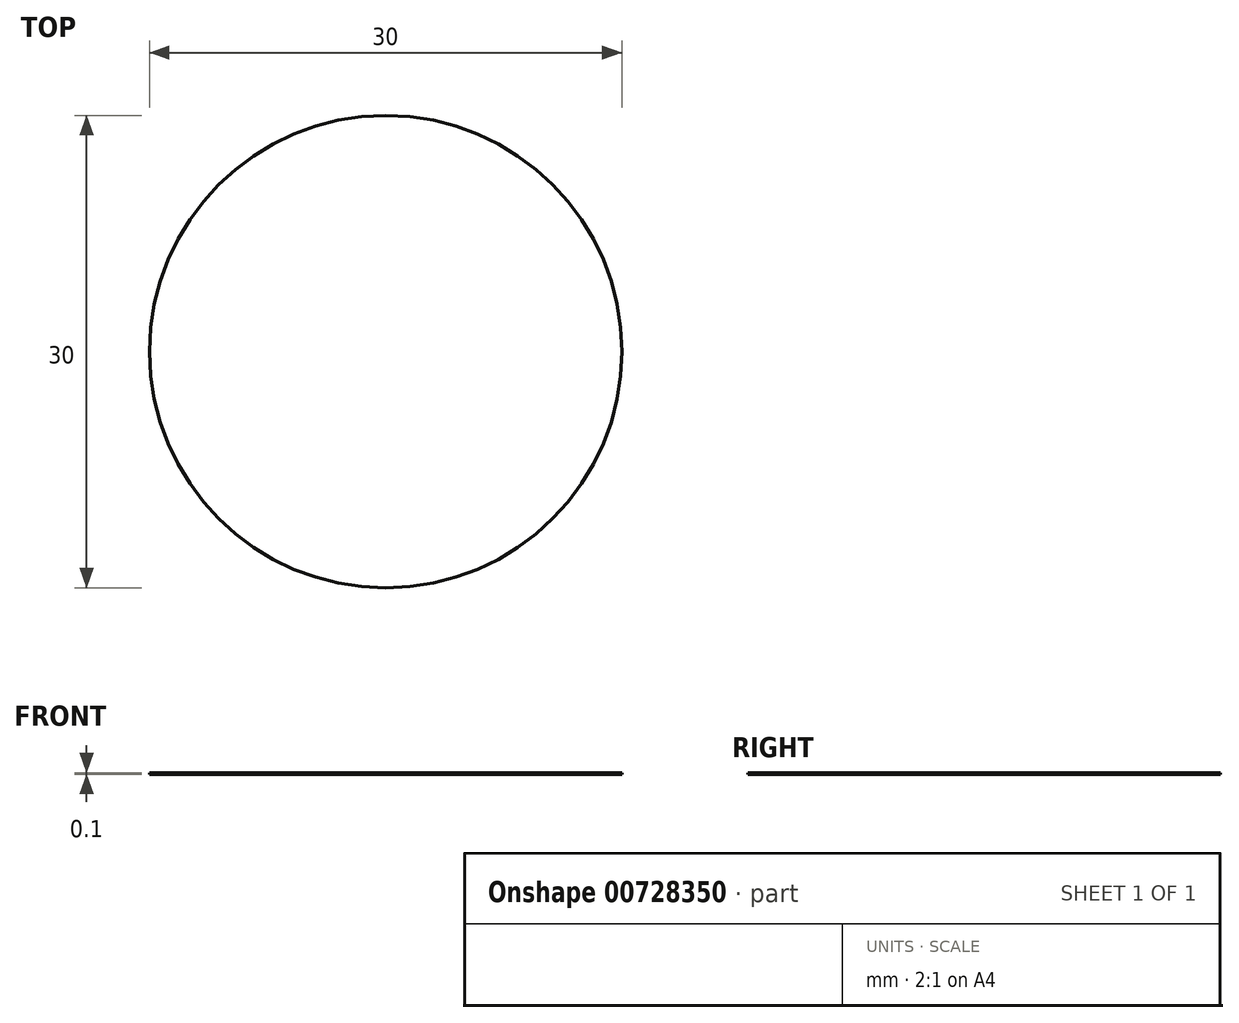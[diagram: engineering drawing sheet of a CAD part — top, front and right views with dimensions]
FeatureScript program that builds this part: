
annotation { "Feature Type Name" : "Feature", "Feature Type Description" : "" }
export const myFeature = defineFeature(function(context is Context, id is Id, definition is map)
    precondition{}
    {
        {
            var Q0;
            Q0=qCreatedBy(makeId("Top.planeOp"),FACE);
            var sketch = newSketch(context, id + "F0", { "sketchPlane" : qUnion([Q0])});
            skCircle(sketch, "E0", {"center": v(0, 0) * mm, "radius": 15 * mm});
            skSolve(sketch);
        }
        {
            var Q0;
            Q0 = qSketchRegion(id + "F0", true);
            var Q1;
            Q1=makeQuery(id+"F0.imprint","IMPRINT",FACE,{"disambiguationData":[TD([[makeQuery(id+"F0.imprint","IMPRINT",EDGE,{"derivedFrom":sQuery(id+"F0.wireOp",EDGE,"E0")}),1.0]])]});
            extrude(context, id + "F1", {"entities" : qUnion([Q0, Q1]), "depth" : 0.1 * mm, "offsetDistance" : 25 * mm});
        }
    });
